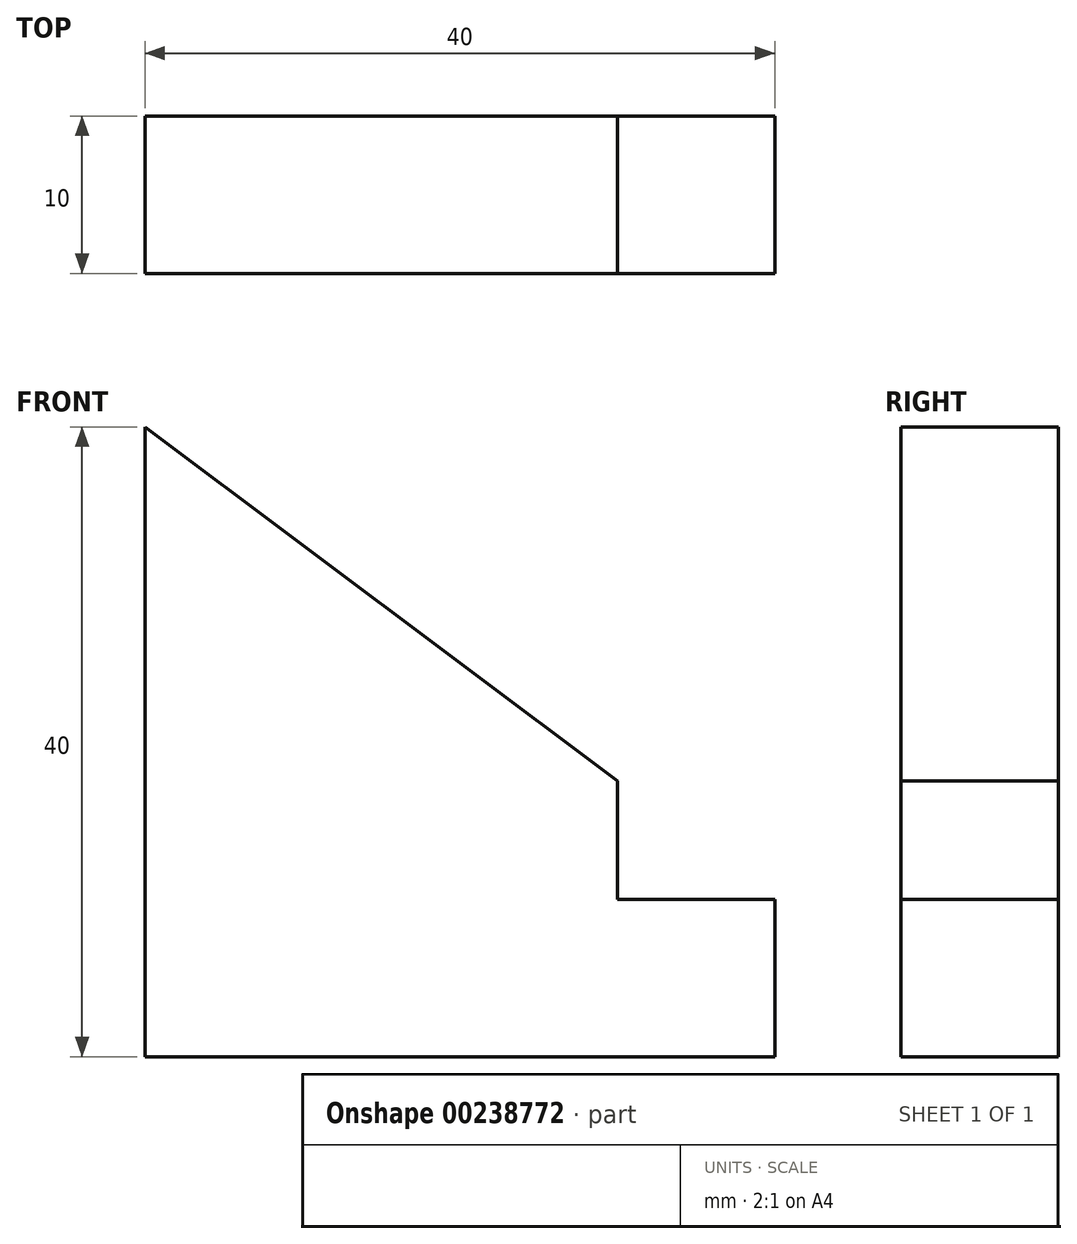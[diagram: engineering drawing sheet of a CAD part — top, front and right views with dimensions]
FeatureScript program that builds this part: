
annotation { "Feature Type Name" : "Feature", "Feature Type Description" : "" }
export const myFeature = defineFeature(function(context is Context, id is Id, definition is map)
    precondition{}
    {
        {
            var Q0;
            Q0=qCreatedBy(makeId("Front.planeOp"),FACE);
            var sketch = newSketch(context, id + "F0", { "sketchPlane" : qUnion([Q0])});
            skLineSegment(sketch, "E0.bottom", {"start": v(20, 20) * mm, "end": v(-20, 20) * mm});
            skLineSegment(sketch, "E0.top", {"start": v(20, -20) * mm, "end": v(-20, -20) * mm});
            skLineSegment(sketch, "E0.left", {"start": v(20, 20) * mm, "end": v(20, -20) * mm});
            skLineSegment(sketch, "E0.right", {"start": v(-20, 20) * mm, "end": v(-20, -20) * mm});
            skPoint(sketch, "E0.middle", {"position": v(0, 0) * mm});
            skPoint(sketch, "E1", {"position": v(20, -10) * mm});
            skLineSegment(sketch, "E2", {"start": v(-20, 20) * mm, "end": v(20, -10) * mm});
            skLineSegment(sketch, "E3", {"start": v(20, -10) * mm, "end": v(-20, -10) * mm});
            skPoint(sketch, "E4", {"position": v(10, -10) * mm});
            skLineSegment(sketch, "E5", {"start": v(10, -10) * mm, "end": v(10, 20) * mm});
            skSolve(sketch);
        }
        {
            var Q0;
            {var subQ1=sQuery(id+"F0.wireOp",EDGE,"E0.right");var subQ3=sQuery(id+"F0.wireOp",EDGE,"E3");var subQ4=makeQuery(id+"F0.imprint","INTERSECT",VERTEX,{"derivedFrom":[subQ1,subQ3]});Q0=makeQuery(id+"F0.imprint","IMPRINT",FACE,{"disambiguationData":[TD([[makeQuery(id+"F0.imprint","IMPRINT",EDGE,{"disambiguationData":[TD([[subQ4,1.0]])],"derivedFrom":subQ3}),-1.0]])]});}
            var Q1;
            {var subQ4=sQuery(id+"F0.wireOp",EDGE,"E0.top");Q1=makeQuery(id+"F0.imprint","IMPRINT",FACE,{"disambiguationData":[TD([[makeQuery(id+"F0.imprint","IMPRINT",EDGE,{"derivedFrom":subQ4}),-1.0]])]});}
            extrude(context, id + "F1", {"entities" : qUnion([Q0, Q1]), "endBound" : BoundingType.SYMMETRIC, "depth" : 10 * mm});
        }
    });
